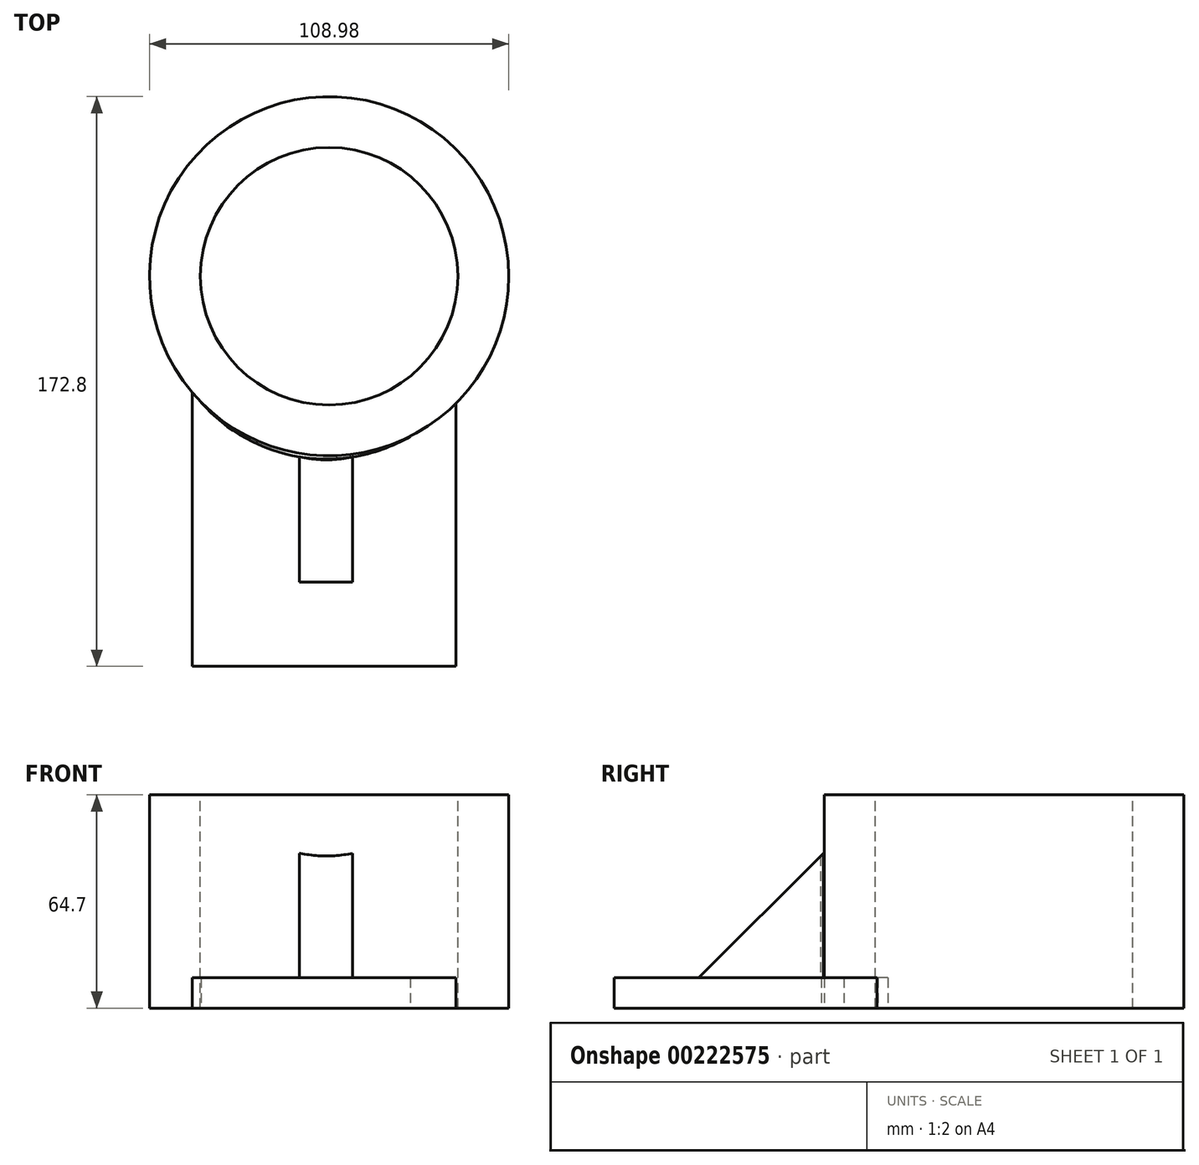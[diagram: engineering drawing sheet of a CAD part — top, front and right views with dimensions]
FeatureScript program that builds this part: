
annotation { "Feature Type Name" : "Feature", "Feature Type Description" : "" }
export const myFeature = defineFeature(function(context is Context, id is Id, definition is map)
    precondition{}
    {
        {
            var Q0;
            Q0=qCreatedBy(makeId("Top.planeOp"),FACE);
            var sketch = newSketch(context, id + "F0", { "sketchPlane" : qUnion([Q0])});
            skCircle(sketch, "E0", {"center": v(0, 42.4) * mm, "radius": 54.49 * mm});
            skSolve(sketch);
        }
        {
            var Q0;
            Q0 = qSketchRegion(id + "F0", true);
            extrude(context, id + "F1", {"entities" : qUnion([Q0]), "depth" : 64.7 * mm});
        }
        {
            var Q0;
            Q0=makeQuery(id+"F1.opExtrude","CAP_FACE",FACE,{"disambiguationData":[OSD([sQuery(id+"F0.wireOp",EDGE,"E0")])],"isStart":false});
            var sketch = newSketch(context, id + "F2", { "sketchPlane" : qUnion([Q0])});
            skCircle(sketch, "E1", {"center": v(0, 42.4) * mm, "radius": 39.06 * mm});
            skSolve(sketch);
        }
        {
            var Q0;
            Q0 = qSketchRegion(id + "F2", true);
            extrude(context, id + "F3", {"entities" : qUnion([Q0]), "operationType" : NewBodyOperationType.REMOVE, "endBound" : BoundingType.THROUGH_ALL, "oppositeDirection" : true, "depth" : 25.4 * mm});
        }
        {
            var Q0;
            Q0=qCreatedBy(makeId("Top.planeOp"),FACE);
            var sketch = newSketch(context, id + "F4", { "sketchPlane" : qUnion([Q0])});
            skLineSegment(sketch, "E2", {"start": v(-41.54, 7.55) * mm, "end": v(-41.54, -75.91) * mm});
            skLineSegment(sketch, "E3", {"start": v(-41.54, -75.91) * mm, "end": v(38.47, -75.91) * mm});
            skLineSegment(sketch, "E4", {"start": v(38.47, -75.91) * mm, "end": v(38.47, 5.62) * mm});
            skArc(sketch, "E5", {"start": v(-41.54, 7.55) * mm, "mid": v(-2, -13.03) * mm, "end": v(38.47, 5.62) * mm});
            skSolve(sketch);
        }
        {
            var Q0;
            Q0 = qSketchRegion(id + "F4", true);
            extrude(context, id + "F5", {"entities" : qUnion([Q0]), "operationType" : NewBodyOperationType.ADD, "depth" : 9.18 * mm});
        }
        {
            var Q0;
            Q0=makeQuery(id+"F5.opExtrude","CAP_FACE",FACE,{"disambiguationData":[OSD([sQuery(id+"F4.wireOp",EDGE,"E2"),sQuery(id+"F4.wireOp",EDGE,"E3"),sQuery(id+"F4.wireOp",EDGE,"E4"),sQuery(id+"F4.wireOp",EDGE,"E5")])],"isStart":false});
            var sketch = newSketch(context, id + "F6", { "sketchPlane" : qUnion([Q0])});
            skLineSegment(sketch, "E6", {"start": v(-8.95, -12.38) * mm, "end": v(-8.95, -50.31) * mm});
            skLineSegment(sketch, "E7", {"start": v(-8.95, -50.31) * mm, "end": v(7.18, -50.31) * mm});
            skLineSegment(sketch, "E8", {"start": v(7.18, -50.31) * mm, "end": v(7.18, -12.41) * mm});
            skArc(sketch, "E9", {"start": v(-8.95, -12.38) * mm, "mid": v(-0.89, -13.28) * mm, "end": v(7.18, -12.41) * mm});
            skSolve(sketch);
        }
        {
            var Q0;
            Q0 = qSketchRegion(id + "F6", true);
            extrude(context, id + "F7", {"entities" : qUnion([Q0]), "operationType" : NewBodyOperationType.ADD, "depth" : 37.81 * mm});
        }
        {
            var Q0;
            Q0=makeQuery(id+"F7.opExtrude","SWEPT_FACE",FACE,{"disambiguationData":[OSD([sQuery(id+"F6.wireOp",EDGE,"E8")])]});
            var sketch = newSketch(context, id + "F8", { "sketchPlane" : qUnion([Q0])});
            skLineSegment(sketch, "E10", {"start": v(-12.41, 47) * mm, "end": v(-50.31, 9.18) * mm});
            skSolve(sketch);
        }
        {
            var Q0;
            Q0=makeQuery(id+"F8.imprint","IMPRINT",FACE,{"disambiguationData":[TD([[makeQuery(id+"F8.imprint","IMPRINT",EDGE,{"derivedFrom":sQuery(id+"F8.wireOp",EDGE,"E10")}),-1.0]])]});
            extrude(context, id + "F9", {"entities" : qUnion([Q0]), "operationType" : NewBodyOperationType.REMOVE, "endBound" : BoundingType.THROUGH_ALL, "oppositeDirection" : true, "depth" : 25.4 * mm});
        }
    });
